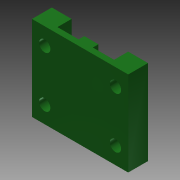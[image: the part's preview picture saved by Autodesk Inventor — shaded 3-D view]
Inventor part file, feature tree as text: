
AUTODESK INVENTOR PART (.ipt)
format: ipt  version: 2015 SP1 (Build 190203100, 203)  size: 109,568 bytes
history: native  units: mm
features: extrude x3, sketch x1, hole x1, pattern_linear x1
ambient origin geometry x8: Origin, YZ Plane, XZ Plane, XY Plane, X Axis, Y Axis, Z Axis, Center Point
bodies: Solid1 (feature_tree)
feature tree (6):
  sketch  "Sketch1"  dims[d0=20.0mm d1=5.0mm d2=34.0mm d3=30.0mm d4=6.0mm d5=4.5mm d6=2.0mm d7=0.0mm d8=7.0mm d9=0.0mm d10=4.0mm d11=0.0mm d12=4.0mm d13=6.0mm d14=4.0mm d15=2.0mm d16=90.0deg d17=8.0mm d18=20.594885mm d19=20.0mm d21=18.0mm d22=20.0mm d24=25.0mm]
  extrude  "Extrusion1"  Depth=5.0mm
  extrude  "Extrusion2"  Depth=34.0mm
  extrude  "Extrusion3"  Depth=30.0mm
  hole  "Hole1"  [1 undecoded]
  pattern_linear  "Rectangular Pattern1"  Spacing1=4.5mm  [1 undecoded]
note: 2 required parameter values undecoded (feature->parameter linkage not recoverable at this tier; creation-order binding heuristic only, values carry confidence <= 0.55)
